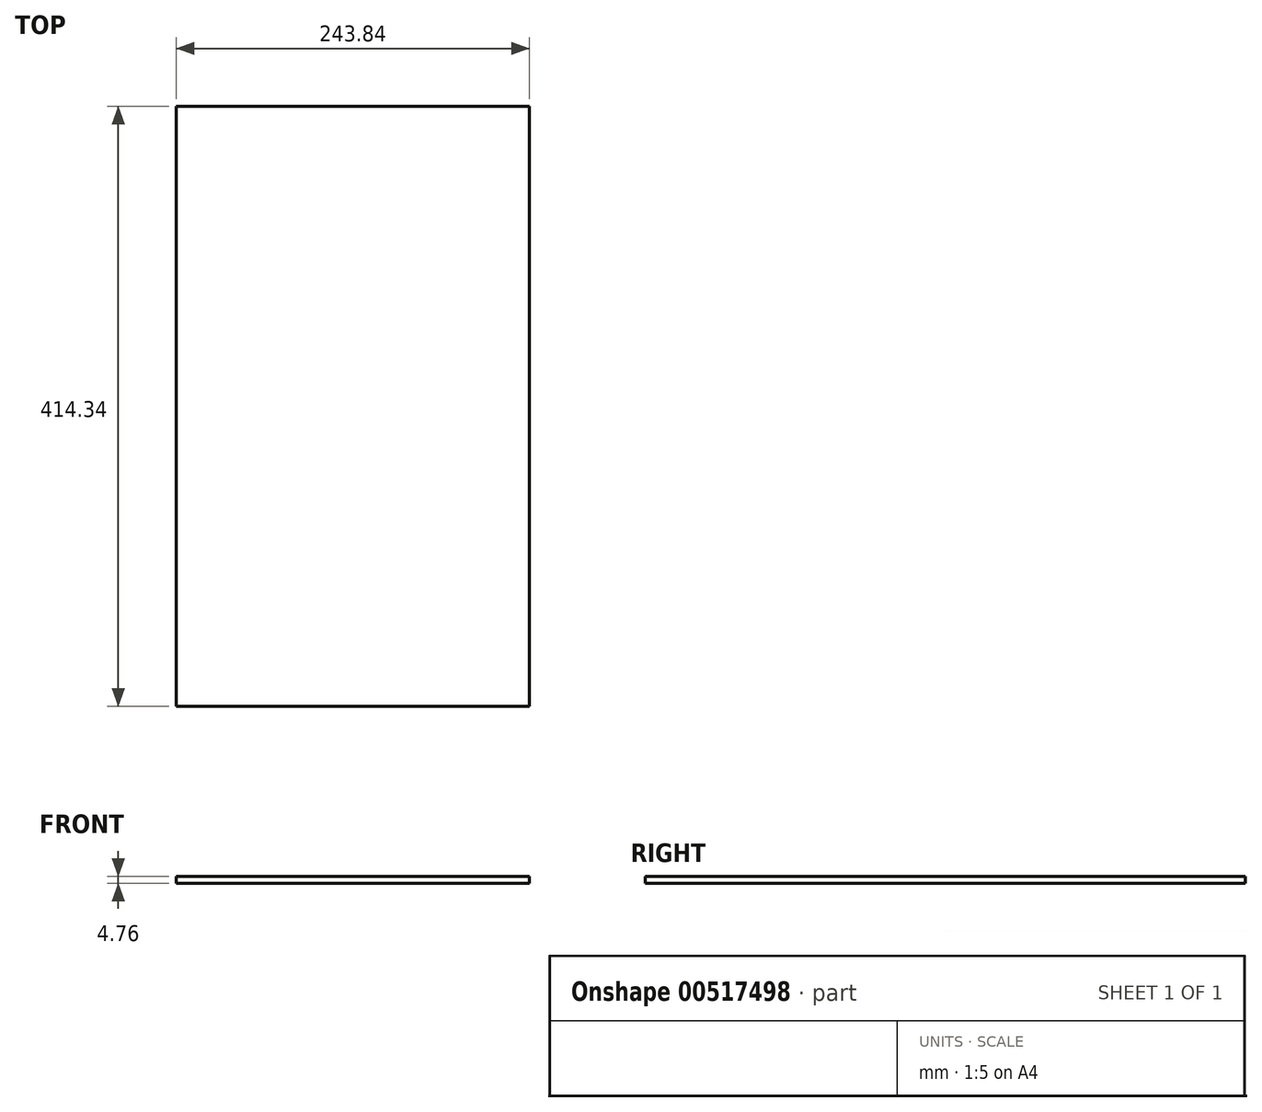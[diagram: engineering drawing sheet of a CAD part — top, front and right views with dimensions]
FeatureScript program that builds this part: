
annotation { "Feature Type Name" : "Feature", "Feature Type Description" : "" }
export const myFeature = defineFeature(function(context is Context, id is Id, definition is map)
    precondition{}
    {
        {
            var Q0;
            Q0=qCreatedBy(makeId("Top.planeOp"),FACE);
            var sketch = newSketch(context, id + "F0", { "sketchPlane" : qUnion([Q0])});
            skLineSegment(sketch, "E0.bottom", {"start": v(-121.92, 207.17) * mm, "end": v(121.92, 207.17) * mm});
            skLineSegment(sketch, "E0.top", {"start": v(-121.92, -207.17) * mm, "end": v(121.92, -207.17) * mm});
            skLineSegment(sketch, "E0.left", {"start": v(-121.92, 207.17) * mm, "end": v(-121.92, -207.17) * mm});
            skLineSegment(sketch, "E0.right", {"start": v(121.92, 207.17) * mm, "end": v(121.92, -207.17) * mm});
            skPoint(sketch, "E0.middle", {"position": v(0, 0) * mm});
            skSolve(sketch);
        }
        {
            var Q0;
            Q0 = qSketchRegion(id + "F0", true);
            extrude(context, id + "F1", {"entities" : qUnion([Q0]), "depth" : 4.76 * mm, "offsetDistance" : 25.4 * mm});
        }
    });
